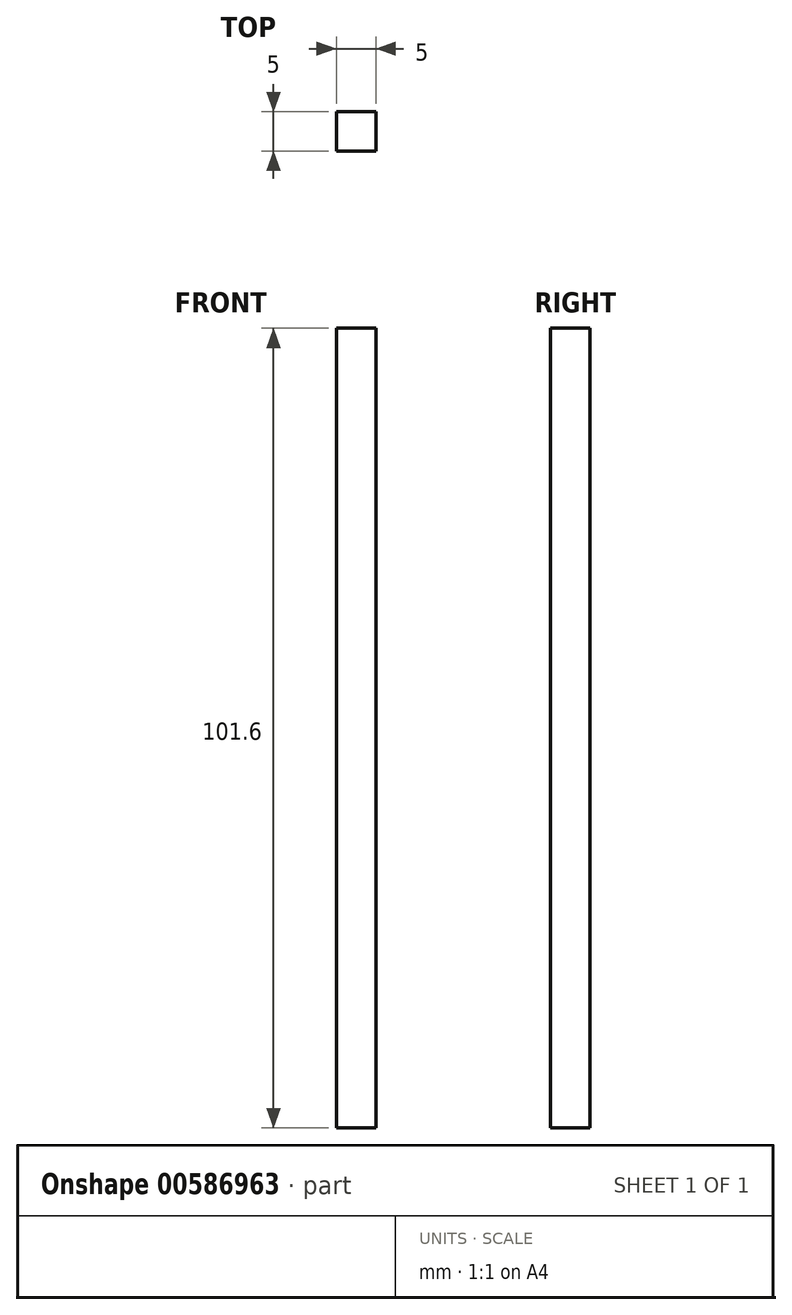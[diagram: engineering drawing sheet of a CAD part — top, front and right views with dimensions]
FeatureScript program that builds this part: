
annotation { "Feature Type Name" : "Feature", "Feature Type Description" : "" }
export const myFeature = defineFeature(function(context is Context, id is Id, definition is map)
    precondition{}
    {
        {
            var Q0;
            Q0=qCreatedBy(makeId("Top.planeOp"),FACE);
            var sketch = newSketch(context, id + "F0", { "sketchPlane" : qUnion([Q0])});
            skLineSegment(sketch, "E0.bottom", {"start": v(2.5, 2.5) * mm, "end": v(-2.5, 2.5) * mm});
            skLineSegment(sketch, "E0.top", {"start": v(2.5, -2.5) * mm, "end": v(-2.5, -2.5) * mm});
            skLineSegment(sketch, "E0.left", {"start": v(2.5, 2.5) * mm, "end": v(2.5, -2.5) * mm});
            skLineSegment(sketch, "E0.right", {"start": v(-2.5, 2.5) * mm, "end": v(-2.5, -2.5) * mm});
            skPoint(sketch, "E0.middle", {"position": v(0, 0) * mm});
            skSolve(sketch);
        }
        {
            var Q0;
            Q0=makeQuery(id+"F0.imprint","IMPRINT",FACE,{"disambiguationData":[TD([[makeQuery(id+"F0.imprint","IMPRINT",EDGE,{"derivedFrom":sQuery(id+"F0.wireOp",EDGE,"E0.bottom")}),1.0]])]});
            extrude(context, id + "F1", {"entities" : qUnion([Q0]), "depth" : 101.6 * mm, "offsetDistance" : 25.4 * mm});
        }
    });
